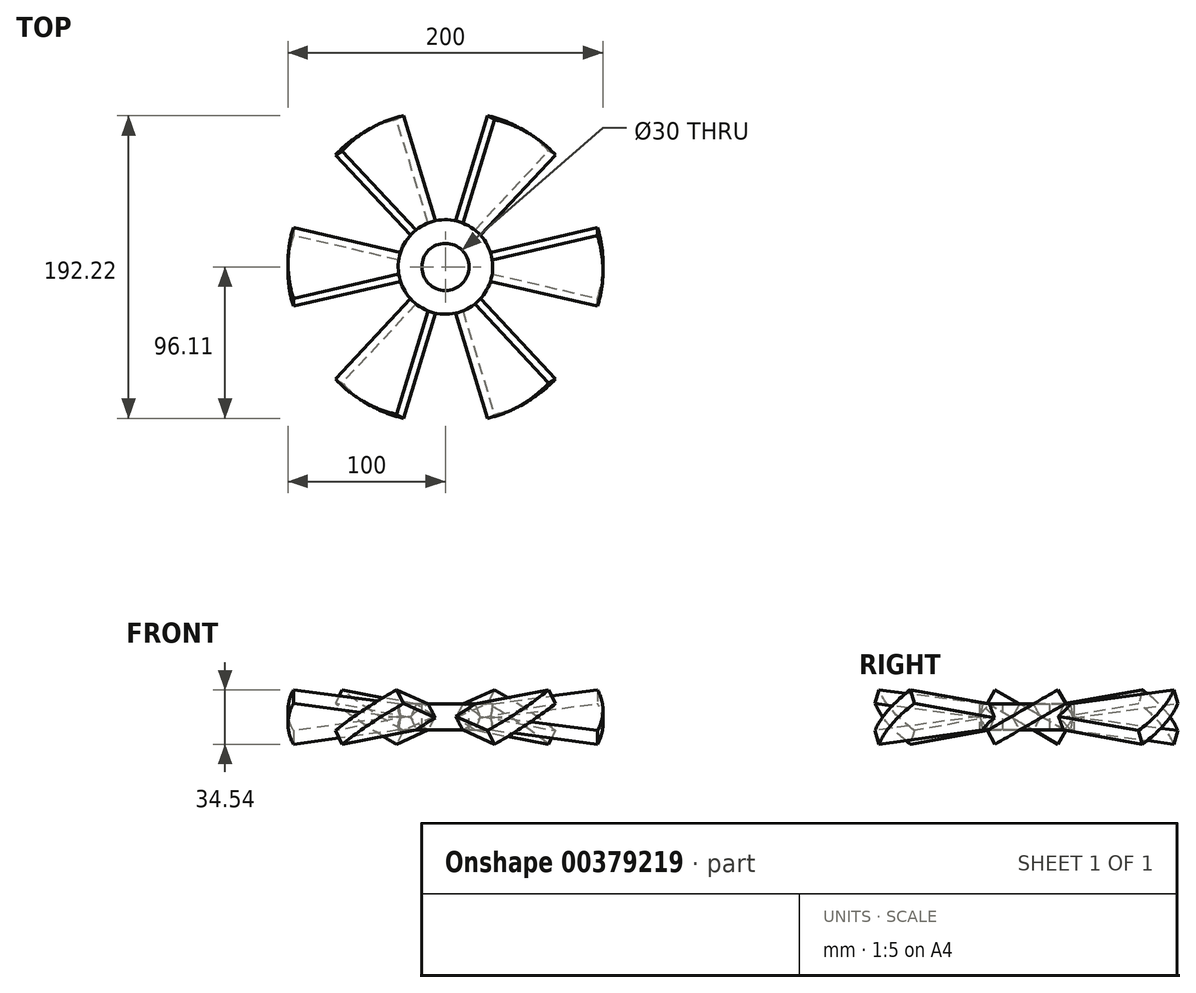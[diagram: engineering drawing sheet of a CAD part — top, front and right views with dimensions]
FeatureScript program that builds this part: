
annotation { "Feature Type Name" : "Feature", "Feature Type Description" : "" }
export const myFeature = defineFeature(function(context is Context, id is Id, definition is map)
    precondition{}
    {
        {
            var Q0;
            Q0=qCreatedBy(makeId("Top.planeOp"),FACE);
            var sketch = newSketch(context, id + "F0", { "sketchPlane" : qUnion([Q0])});
            skLineSegment(sketch, "E0", {"start": v(0, 0) * mm, "end": v(96.6, 25.88) * mm});
            skArc(sketch, "E1", {"start": v(96.6, 25.88) * mm, "mid": v(100, 0) * mm, "end": v(96.6, -25.88) * mm});
            skLineSegment(sketch, "E2", {"start": v(0, 0) * mm, "end": v(96.6, -25.88) * mm});
            skLineSegment(sketch, "E3", {"start": v(0, 0) * mm, "end": v(140.3, 0) * mm, "construction": true});
            skSolve(sketch);
        }
        {
            var Q0;
            Q0=makeQuery(id+"F0.imprint","IMPRINT",FACE,{"disambiguationData":[TD([[makeQuery(id+"F0.imprint","IMPRINT",EDGE,{"derivedFrom":sQuery(id+"F0.wireOp",EDGE,"E0")}),-1.0]])]});
            extrude(context, id + "F1", {"entities" : qUnion([Q0]), "endBound" : BoundingType.SYMMETRIC, "depth" : 10 * mm});
        }
        {
            var Q0;
            Q0=makeQuery(id+"F1.opExtrude","SWEPT_BODY",BODY,{"disambiguationData":[OSD([sQuery(id+"F0.wireOp",EDGE,"E0"),sQuery(id+"F0.wireOp",EDGE,"E1"),sQuery(id+"F0.wireOp",EDGE,"E2")])]});
            var Q1;
            Q1=sQuery(id+"F0.wireOp",EDGE,"E3");
            transform(context, id + "F2", {"entities" : qUnion([Q0]), "transformType" : TransformType.ROTATION, "transformAxis" : qUnion([Q1]), "angle" : 30 * degree, "makeCopy" : false});
        }
        {
            var Q0;
            Q0=qCreatedBy(makeId("Front.planeOp"),FACE);
            var sketch = newSketch(context, id + "F3", { "sketchPlane" : qUnion([Q0])});
            skLineSegment(sketch, "E4", {"start": v(0, 0) * mm, "end": v(0, 67.37) * mm, "construction": true});
            skSolve(sketch);
        }
        {
            var Q0;
            Q0=makeQuery(id+"F1.opExtrude","SWEPT_BODY",BODY,{"disambiguationData":[OSD([sQuery(id+"F0.wireOp",EDGE,"E0"),sQuery(id+"F0.wireOp",EDGE,"E1"),sQuery(id+"F0.wireOp",EDGE,"E2")])]});
            var Q1;
            Q1=sQuery(id+"F3.wireOp",EDGE,"E4");
            circularPattern(context, id + "F4", {"entities" : qUnion([Q0]), "axis" : qUnion([Q1]), "angle" : 360 * degree, "instanceCount" : 6, "equalSpace" : true});
        }
        {
            var Q0;
            Q0=qCreatedBy(makeId("Top.planeOp"),FACE);
            var sketch = newSketch(context, id + "F5", { "sketchPlane" : qUnion([Q0])});
            skCircle(sketch, "E5", {"center": v(0, 0) * mm, "radius": 30 * mm});
            skSolve(sketch);
        }
        {
            var Q0;
            Q0 = qSketchRegion(id + "F5", true);
            extrude(context, id + "F6", {"entities" : qUnion([Q0]), "endBound" : BoundingType.SYMMETRIC, "depth" : 25 * mm});
        }
        {
            var Q0;
            Q0=makeQuery(id+"F1.opExtrude","SWEPT_BODY",BODY,{"disambiguationData":[OSD([sQuery(id+"F0.wireOp",EDGE,"E0"),sQuery(id+"F0.wireOp",EDGE,"E1"),sQuery(id+"F0.wireOp",EDGE,"E2")])]});
            var Q1;
            Q1=makeQuery(id+"F4.opPattern","COPY",BODY,{"derivedFrom":makeQuery(id+"F1.opExtrude","SWEPT_BODY",BODY,{"disambiguationData":[OSD([sQuery(id+"F0.wireOp",EDGE,"E0"),sQuery(id+"F0.wireOp",EDGE,"E1"),sQuery(id+"F0.wireOp",EDGE,"E2")])]}),"instanceName":"1"});
            var Q2;
            Q2=makeQuery(id+"F4.opPattern","COPY",BODY,{"derivedFrom":makeQuery(id+"F1.opExtrude","SWEPT_BODY",BODY,{"disambiguationData":[OSD([sQuery(id+"F0.wireOp",EDGE,"E0"),sQuery(id+"F0.wireOp",EDGE,"E1"),sQuery(id+"F0.wireOp",EDGE,"E2")])]}),"instanceName":"2"});
            var Q3;
            Q3=makeQuery(id+"F4.opPattern","COPY",BODY,{"derivedFrom":makeQuery(id+"F1.opExtrude","SWEPT_BODY",BODY,{"disambiguationData":[OSD([sQuery(id+"F0.wireOp",EDGE,"E0"),sQuery(id+"F0.wireOp",EDGE,"E1"),sQuery(id+"F0.wireOp",EDGE,"E2")])]}),"instanceName":"3"});
            var Q4;
            Q4=makeQuery(id+"F4.opPattern","COPY",BODY,{"derivedFrom":makeQuery(id+"F1.opExtrude","SWEPT_BODY",BODY,{"disambiguationData":[OSD([sQuery(id+"F0.wireOp",EDGE,"E0"),sQuery(id+"F0.wireOp",EDGE,"E1"),sQuery(id+"F0.wireOp",EDGE,"E2")])]}),"instanceName":"4"});
            var Q5;
            Q5=makeQuery(id+"F4.opPattern","COPY",BODY,{"derivedFrom":makeQuery(id+"F1.opExtrude","SWEPT_BODY",BODY,{"disambiguationData":[OSD([sQuery(id+"F0.wireOp",EDGE,"E0"),sQuery(id+"F0.wireOp",EDGE,"E1"),sQuery(id+"F0.wireOp",EDGE,"E2")])]}),"instanceName":"5"});
            var Q6;
            Q6=makeQuery(id+"F6.opExtrude","SWEPT_BODY",BODY,{"disambiguationData":[OSD([sQuery(id+"F5.wireOp",EDGE,"E5")])]});
            booleanBodies(context, id + "F7", {"operationType" : BooleanOperationType.UNION, "tools" : qUnion([Q0, Q1, Q2, Q3, Q4, Q5, Q6])});
        }
        {
            var Q0;
            {var subQ0=sQuery(id+"F0.wireOp",EDGE,"E0");Q0=makeQuery(id+"F7.opBoolean","INTERSECT",VERTEX,{"derivedFrom":[makeQuery(id+"F4.opPattern","COPY",FACE,{"derivedFrom":makeQuery(id+"F1.opExtrude","SWEPT_FACE",FACE,{"disambiguationData":[OSD([subQ0])]}),"instanceName":"5"}),makeQuery(id+"F4.opPattern","COPY",FACE,{"derivedFrom":makeQuery(id+"F1.opExtrude","CAP_FACE",FACE,{"disambiguationData":[OSD([subQ0,sQuery(id+"F0.wireOp",EDGE,"E1"),sQuery(id+"F0.wireOp",EDGE,"E2")])],"isStart":false}),"instanceName":"5"}),makeQuery(id+"F6.opExtrude","SWEPT_FACE",FACE,{"disambiguationData":[OSD([sQuery(id+"F5.wireOp",EDGE,"E5")])]})]});}
            var Q1;
            {var subQ0=sQuery(id+"F0.wireOp",EDGE,"E0");Q1=makeQuery(id+"F7.opBoolean","INTERSECT",VERTEX,{"derivedFrom":[makeQuery(id+"F4.opPattern","COPY",FACE,{"derivedFrom":makeQuery(id+"F1.opExtrude","SWEPT_FACE",FACE,{"disambiguationData":[OSD([subQ0])]}),"instanceName":"4"}),makeQuery(id+"F4.opPattern","COPY",FACE,{"derivedFrom":makeQuery(id+"F1.opExtrude","CAP_FACE",FACE,{"disambiguationData":[OSD([subQ0,sQuery(id+"F0.wireOp",EDGE,"E1"),sQuery(id+"F0.wireOp",EDGE,"E2")])],"isStart":false}),"instanceName":"4"}),makeQuery(id+"F6.opExtrude","SWEPT_FACE",FACE,{"disambiguationData":[OSD([sQuery(id+"F5.wireOp",EDGE,"E5")])]})]});}
            var Q2;
            {var subQ0=sQuery(id+"F0.wireOp",EDGE,"E0");Q2=makeQuery(id+"F7.opBoolean","INTERSECT",VERTEX,{"derivedFrom":[makeQuery(id+"F1.opExtrude","SWEPT_FACE",FACE,{"disambiguationData":[OSD([subQ0])]}),makeQuery(id+"F1.opExtrude","CAP_FACE",FACE,{"disambiguationData":[OSD([subQ0,sQuery(id+"F0.wireOp",EDGE,"E1"),sQuery(id+"F0.wireOp",EDGE,"E2")])],"isStart":false}),makeQuery(id+"F6.opExtrude","SWEPT_FACE",FACE,{"disambiguationData":[OSD([sQuery(id+"F5.wireOp",EDGE,"E5")])]})]});}
            cPlane(context, id + "F8", {"entities" : qUnion([Q0, Q1, Q2]), "cplaneType" : CPlaneType.THREE_POINT, "offset" : 25 * mm, "width" : 150 * mm, "height" : 150 * mm});
        }
        {
            var Q0;
            Q0=makeQuery(id+"F6.opExtrude","CAP_FACE",FACE,{"disambiguationData":[OSD([sQuery(id+"F5.wireOp",EDGE,"E5")])],"isStart":false});
            var Q1;
            Q1=qCreatedBy(id+"F8.planeOp",FACE);
            extrude(context, id + "F9", {"entities" : qUnion([Q0]), "operationType" : NewBodyOperationType.REMOVE, "endBound" : BoundingType.UP_TO_SURFACE, "oppositeDirection" : true, "endBoundEntityFace" : qUnion([Q1]), "depth" : 25 * mm});
        }
        {
            var Q0;
            {var subQ0=sQuery(id+"F0.wireOp",EDGE,"E2");Q0=makeQuery(id+"F7.opBoolean","INTERSECT",VERTEX,{"derivedFrom":[makeQuery(id+"F4.opPattern","COPY",FACE,{"derivedFrom":makeQuery(id+"F1.opExtrude","CAP_FACE",FACE,{"disambiguationData":[OSD([sQuery(id+"F0.wireOp",EDGE,"E0"),sQuery(id+"F0.wireOp",EDGE,"E1"),subQ0])],"isStart":true}),"instanceName":"5"}),makeQuery(id+"F4.opPattern","COPY",FACE,{"derivedFrom":makeQuery(id+"F1.opExtrude","SWEPT_FACE",FACE,{"disambiguationData":[OSD([subQ0])]}),"instanceName":"5"}),makeQuery(id+"F6.opExtrude","SWEPT_FACE",FACE,{"disambiguationData":[OSD([sQuery(id+"F5.wireOp",EDGE,"E5")])]})]});}
            var Q1;
            {var subQ0=sQuery(id+"F0.wireOp",EDGE,"E2");Q1=makeQuery(id+"F7.opBoolean","INTERSECT",VERTEX,{"derivedFrom":[makeQuery(id+"F1.opExtrude","CAP_FACE",FACE,{"disambiguationData":[OSD([sQuery(id+"F0.wireOp",EDGE,"E0"),sQuery(id+"F0.wireOp",EDGE,"E1"),subQ0])],"isStart":true}),makeQuery(id+"F1.opExtrude","SWEPT_FACE",FACE,{"disambiguationData":[OSD([subQ0])]}),makeQuery(id+"F6.opExtrude","SWEPT_FACE",FACE,{"disambiguationData":[OSD([sQuery(id+"F5.wireOp",EDGE,"E5")])]})]});}
            var Q2;
            {var subQ0=sQuery(id+"F0.wireOp",EDGE,"E2");Q2=makeQuery(id+"F7.opBoolean","INTERSECT",VERTEX,{"derivedFrom":[makeQuery(id+"F4.opPattern","COPY",FACE,{"derivedFrom":makeQuery(id+"F1.opExtrude","CAP_FACE",FACE,{"disambiguationData":[OSD([sQuery(id+"F0.wireOp",EDGE,"E0"),sQuery(id+"F0.wireOp",EDGE,"E1"),subQ0])],"isStart":true}),"instanceName":"1"}),makeQuery(id+"F4.opPattern","COPY",FACE,{"derivedFrom":makeQuery(id+"F1.opExtrude","SWEPT_FACE",FACE,{"disambiguationData":[OSD([subQ0])]}),"instanceName":"1"}),makeQuery(id+"F6.opExtrude","SWEPT_FACE",FACE,{"disambiguationData":[OSD([sQuery(id+"F5.wireOp",EDGE,"E5")])]})]});}
            cPlane(context, id + "F10", {"entities" : qUnion([Q0, Q1, Q2]), "cplaneType" : CPlaneType.THREE_POINT, "offset" : 25 * mm, "width" : 150 * mm, "height" : 150 * mm});
        }
        {
            var Q0;
            Q0=makeQuery(id+"F6.opExtrude","CAP_FACE",FACE,{"disambiguationData":[OSD([sQuery(id+"F5.wireOp",EDGE,"E5")])],"isStart":true});
            var Q1;
            Q1=qCreatedBy(id+"F10.planeOp",FACE);
            extrude(context, id + "F11", {"entities" : qUnion([Q0]), "operationType" : NewBodyOperationType.REMOVE, "endBound" : BoundingType.UP_TO_SURFACE, "oppositeDirection" : true, "endBoundEntityFace" : qUnion([Q1]), "depth" : 25 * mm});
        }
        {
            var Q0;
            Q0=qCreatedBy(makeId("Top.planeOp"),FACE);
            var sketch = newSketch(context, id + "F12", { "sketchPlane" : qUnion([Q0])});
            skCircle(sketch, "E6", {"center": v(0, 0) * mm, "radius": 15 * mm});
            skSolve(sketch);
        }
        {
            var Q0;
            Q0 = qSketchRegion(id + "F12", true);
            extrude(context, id + "F13", {"entities" : qUnion([Q0]), "operationType" : NewBodyOperationType.REMOVE, "endBound" : BoundingType.SYMMETRIC, "oppositeDirection" : true, "depth" : 25 * mm});
        }
    });
